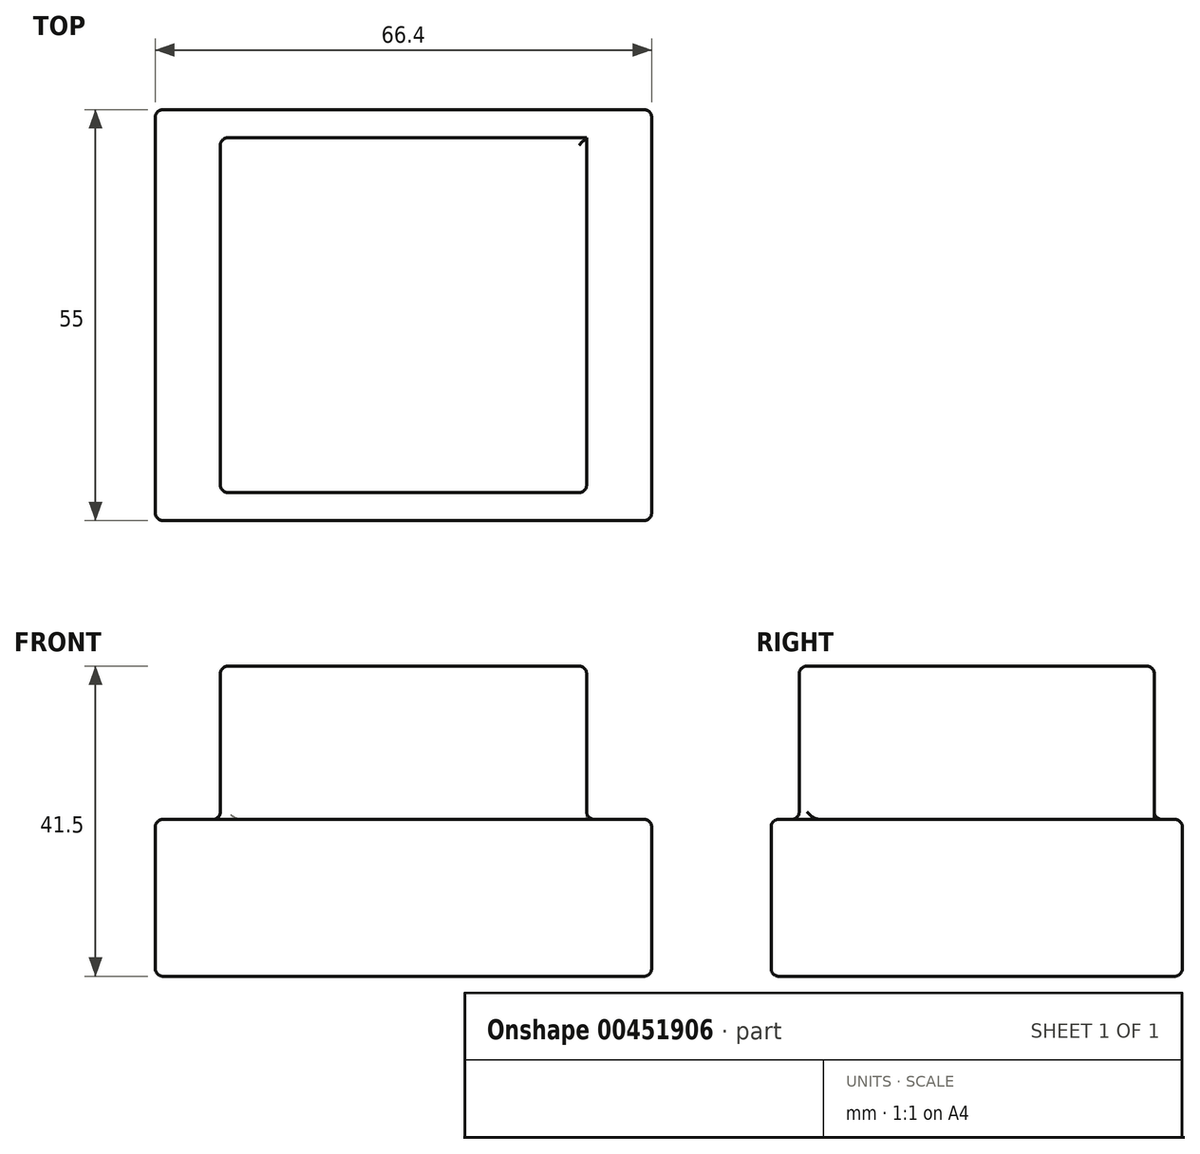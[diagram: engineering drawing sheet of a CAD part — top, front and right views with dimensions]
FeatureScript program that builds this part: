
annotation { "Feature Type Name" : "Feature", "Feature Type Description" : "" }
export const myFeature = defineFeature(function(context is Context, id is Id, definition is map)
    precondition{}
    {
        {
            var Q0;
            Q0=qCreatedBy(makeId("Top.planeOp"),FACE);
            var sketch = newSketch(context, id + "F0", { "sketchPlane" : qUnion([Q0])});
            skLineSegment(sketch, "E0.bottom", {"start": v(-33.2, 27.5) * mm, "end": v(33.2, 27.5) * mm});
            skLineSegment(sketch, "E0.top", {"start": v(-33.2, -27.5) * mm, "end": v(33.2, -27.5) * mm});
            skLineSegment(sketch, "E0.left", {"start": v(-33.2, 27.5) * mm, "end": v(-33.2, -27.5) * mm});
            skLineSegment(sketch, "E0.right", {"start": v(33.2, 27.5) * mm, "end": v(33.2, -27.5) * mm});
            skPoint(sketch, "E0.middle", {"position": v(0, 0) * mm});
            skLineSegment(sketch, "E1.bottom", {"start": v(-24.5, 23.75) * mm, "end": v(24.5, 23.75) * mm});
            skLineSegment(sketch, "E1.top", {"start": v(-24.5, -23.75) * mm, "end": v(24.5, -23.75) * mm});
            skLineSegment(sketch, "E1.left", {"start": v(-24.5, 23.75) * mm, "end": v(-24.5, -23.75) * mm});
            skLineSegment(sketch, "E1.right", {"start": v(24.5, 23.75) * mm, "end": v(24.5, -23.75) * mm});
            skSolve(sketch);
        }
        {
            var Q0;
            Q0 = qSketchRegion(id + "F0", true);
            extrude(context, id + "F1", {"entities" : qUnion([Q0]), "depth" : 21 * mm});
        }
        {
            var Q0;
            Q0=makeQuery(id+"F0.imprint","IMPRINT",FACE,{"disambiguationData":[TD([[makeQuery(id+"F0.imprint","IMPRINT",EDGE,{"derivedFrom":sQuery(id+"F0.wireOp",EDGE,"E1.bottom")}),-1.0]])]});
            extrude(context, id + "F2", {"entities" : qUnion([Q0]), "operationType" : NewBodyOperationType.ADD, "depth" : 41.5 * mm});
        }
        {
            var Q0;
            Q0=makeQuery(id+"F2.opExtrude","CAP_FACE",FACE,{"disambiguationData":[OSD([sQuery(id+"F0.wireOp",EDGE,"E1.bottom"),sQuery(id+"F0.wireOp",EDGE,"E1.top"),sQuery(id+"F0.wireOp",EDGE,"E1.left"),sQuery(id+"F0.wireOp",EDGE,"E1.right")])],"isStart":false});
            var Q1;
            Q1=makeQuery(id+"F2.opExtrude","SWEPT_FACE",FACE,{"disambiguationData":[OSD([sQuery(id+"F0.wireOp",EDGE,"E1.left")])]});
            var Q2;
            Q2=makeQuery(id+"F2.opExtrude","SWEPT_FACE",FACE,{"disambiguationData":[OSD([sQuery(id+"F0.wireOp",EDGE,"E1.top")])]});
            var Q3;
            Q3=makeQuery(id+"F1.opExtrude","SWEPT_FACE",FACE,{"disambiguationData":[OSD([sQuery(id+"F0.wireOp",EDGE,"E0.right")])]});
            var Q4;
            Q4=makeQuery(id+"F1.opExtrude","SWEPT_FACE",FACE,{"disambiguationData":[OSD([sQuery(id+"F0.wireOp",EDGE,"E0.top")])]});
            var Q5;
            Q5=makeQuery(id+"F1.opExtrude","SWEPT_FACE",FACE,{"disambiguationData":[OSD([sQuery(id+"F0.wireOp",EDGE,"E0.left")])]});
            var Q6;
            Q6=makeQuery(id+"F1.opExtrude","SWEPT_FACE",FACE,{"disambiguationData":[OSD([sQuery(id+"F0.wireOp",EDGE,"E0.bottom")])]});
            var Q7;
            Q7=makeQuery(id+"F1.opExtrude","CAP_EDGE",EDGE,{"disambiguationData":[OSD([sQuery(id+"F0.wireOp",EDGE,"E1.right")])],"isStart":false});
            fillet(context, id + "F3", {"entities" : qUnion([Q0, Q1, Q2, Q3, Q4, Q5, Q6, Q7]), "radius" : 1 * mm, "tangentPropagation" : true, "allowEdgeOverflow" : false});
        }
    });
